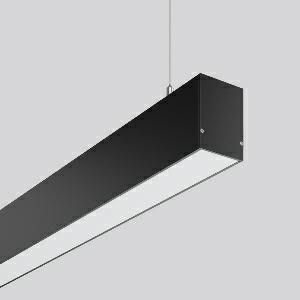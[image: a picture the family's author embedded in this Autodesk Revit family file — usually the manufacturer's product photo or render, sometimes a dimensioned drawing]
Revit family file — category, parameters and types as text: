
# Revit family: less_is_more_50_312313_003_1_1fba
name_source: partatom
category: Lighting Fixtures
units: mm (PartAtom-declared; Revit-internal decimal feet)

## family parameters
Cut with Voids When Loaded = No
Host = Face
Light Source = No
Part Type = Normal
Room Calculation Point = No
Round Connector Dimension = Use Diameter
Shared = No

## types (1)
- LESS IS MORE 50 (1 x LED Modul 840, 4050 lm, 4000)
    Apparent Load = 34 VA
    CIE Flux Codes = 48 79 95 100 100
    Color Rendering = 80
    Color Temperature = 4000
    Default Elevation = 1800 mm
    Description = Series: LESS IS MORE 50
Linear pendant luminaire for aesthetically sophisticated lighting. Housing: extruded aluminium profile, powder-coated. End cap aluminium powder-coated. Canopy made of aluminium, powder-coated. Diffuser made of non-yellowing plastic (PMMA), opal. Direct light emission. Suitable for pendant. 2-point steel cable suspension freely positionable and infinitely height-adjustable. Special lengths available on request. LED unit with integrated converter interchangeable and removable. Suitable for through-wiring. With sensors or as a safety luminaire on request. 
Colour: deep black, matt (RAL 9005)
Length: 1407 mm
Width: 57 mm
Height: 75 mm
Suspension length: 2000 mm
Lamp: LED
Socket: without socket
Colour temperature: 4000K
Colour rendering index (CRI): 80
System power: 34 W
Rated luminous flux: 4050 lm
Luminous efficiency: 119 lm/W
Control gear: Regulated power supply
Protection class: I
Type of protection: IP 20
    Height = 75 mm
    Lamp = 1 x LED Modul 840
    Lamp Light Flux = 4050 lm
    Lamp count = 1
    Length = 1407 mm
    Lifetime = 50000 h
    Luminous efficacy = 119 lm/W
    Manufacturer = RZB
    ModVariant = No
    Model = 312313.003.1
    Mounting Place = Ceiling
    Mounting Type = Pendant
    Number of Poles = 1
    OnlyDefault = Yes
    Power Factor = 1
    Product Name = LESS IS MORE 50
    Product group = Pendant LED linear luminaires
    ProductGroupID = 907
    Protection Class = Protection class I
    Protection Degree = IP 20
    RLX_Detail_Level = 1
    RLX_Emergency_Light_Flux = 0 lm
    RLX_Emergency_Type = 0
    RLX_Emergency_Type_DB = No
    RlxData = <blob elided: 28877 chars, md5=40ece234>
    Socket = socket
    Standby Power = 0 W
    System Light Flux = 4050 lm
    System Power = 34 W
    Type Comments = Product without accessories
    Type Image = 312318.003.jpg
    URL = http://relux.com
    VarID = ---
    Voltage = 230 V
    Voltage Range = 220-240 V
    Weight = 0.00 kg
    Width = 57 mm

## geometry (parser evidence)
native form markers: Blend x4, Sweep x9
no freeform markers — native parametric forms only
